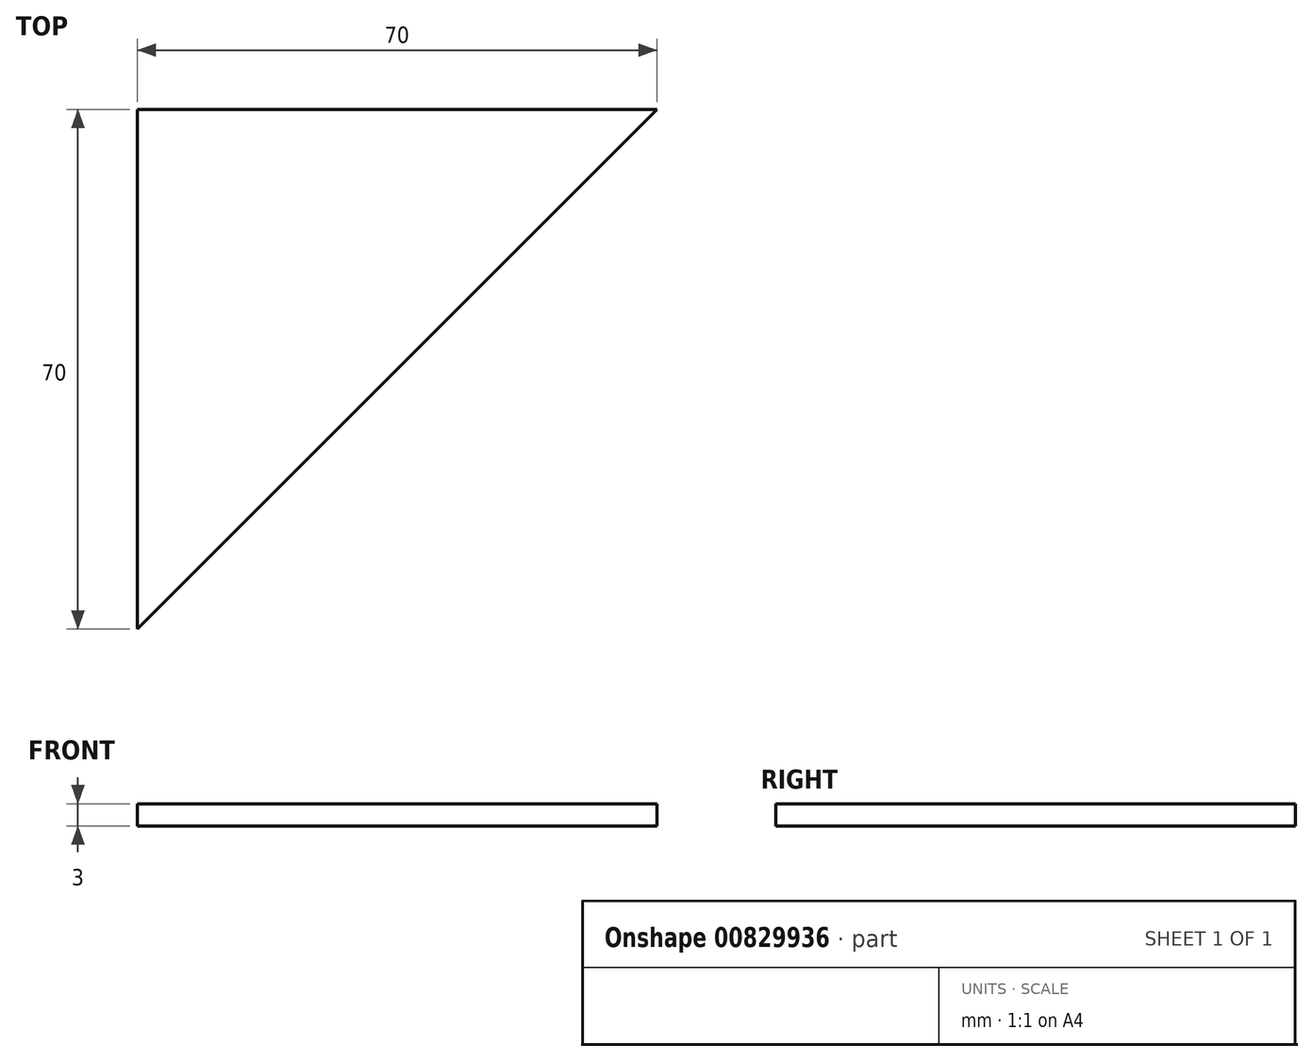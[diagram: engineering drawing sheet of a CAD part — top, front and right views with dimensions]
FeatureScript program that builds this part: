
annotation { "Feature Type Name" : "Feature", "Feature Type Description" : "" }
export const myFeature = defineFeature(function(context is Context, id is Id, definition is map)
    precondition{}
    {
        {
            var Q0;
            Q0=qCreatedBy(makeId("Top.planeOp"),FACE);
            var sketch = newSketch(context, id + "F0", { "sketchPlane" : qUnion([Q0])});
            skLineSegment(sketch, "E0", {"start": v(0, 0) * mm, "end": v(70, 0) * mm});
            skLineSegment(sketch, "E1", {"start": v(0, 0) * mm, "end": v(0, -70) * mm});
            skLineSegment(sketch, "E2", {"start": v(0, -70) * mm, "end": v(70, 0) * mm});
            skSolve(sketch);
        }
        {
            var Q0;
            Q0=makeQuery(id+"F0.imprint","IMPRINT",FACE,{"disambiguationData":[TD([[makeQuery(id+"F0.imprint","IMPRINT",EDGE,{"derivedFrom":sQuery(id+"F0.wireOp",EDGE,"E0")}),-1.0]])]});
            extrude(context, id + "F1", {"entities" : qUnion([Q0]), "depth" : 3 * mm, "offsetDistance" : 25 * mm});
        }
    });
